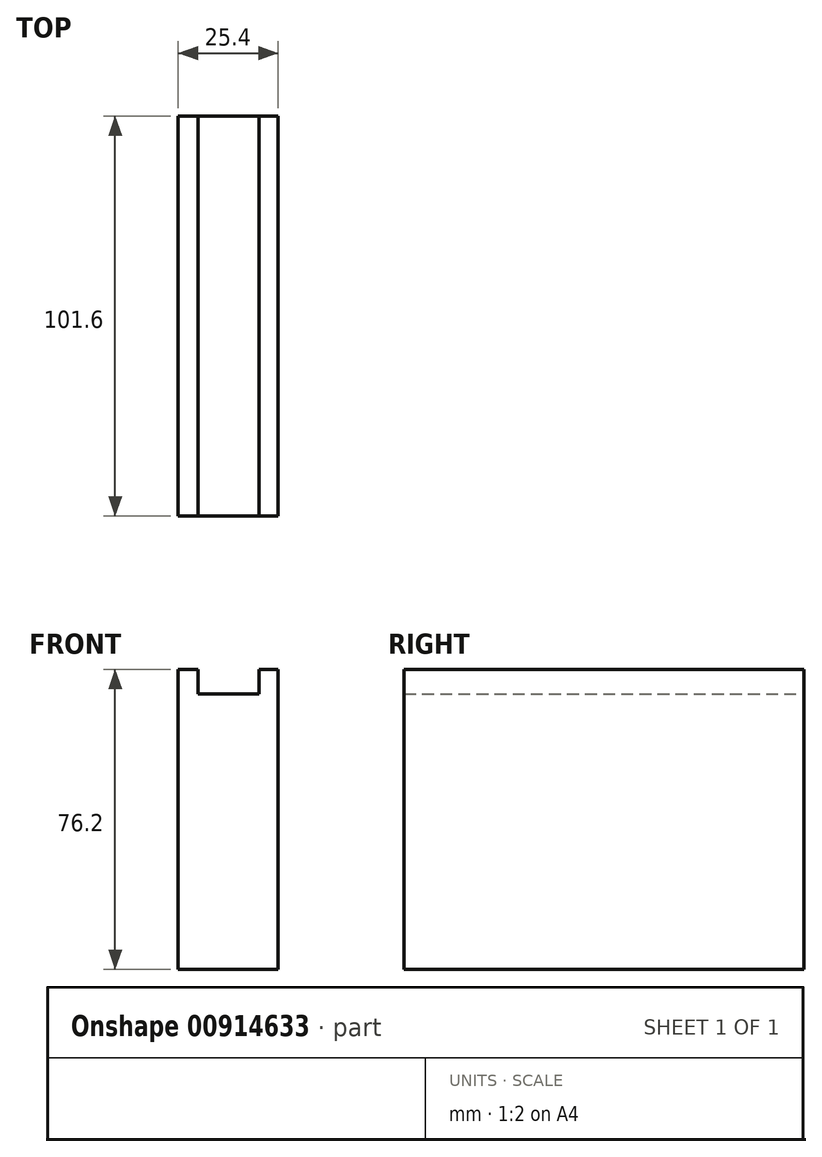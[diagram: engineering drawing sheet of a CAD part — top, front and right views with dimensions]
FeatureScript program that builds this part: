
annotation { "Feature Type Name" : "Feature", "Feature Type Description" : "" }
export const myFeature = defineFeature(function(context is Context, id is Id, definition is map)
    precondition{}
    {
        {
            var Q0;
            Q0=qCreatedBy(makeId("Right.planeOp"),FACE);
            var sketch = newSketch(context, id + "F0", { "sketchPlane" : qUnion([Q0])});
            skLineSegment(sketch, "E0.bottom", {"start": v(-44.25, 27.35) * mm, "end": v(57.35, 27.35) * mm});
            skLineSegment(sketch, "E0.top", {"start": v(-44.25, -48.85) * mm, "end": v(57.35, -48.85) * mm});
            skLineSegment(sketch, "E0.left", {"start": v(-44.25, 27.35) * mm, "end": v(-44.25, -48.85) * mm});
            skLineSegment(sketch, "E0.right", {"start": v(57.35, 27.35) * mm, "end": v(57.35, -48.85) * mm});
            skLineSegment(sketch, "E1.bottom", {"start": v(-44.25, 21.14) * mm, "end": v(57.35, 21.14) * mm});
            skLineSegment(sketch, "E1.left", {"start": v(-44.25, 21.14) * mm, "end": v(-44.25, -48.85) * mm});
            skLineSegment(sketch, "E1.right", {"start": v(57.35, 21.14) * mm, "end": v(57.35, -48.85) * mm});
            skSolve(sketch);
        }
        {
            var Q0;
            Q0 = qSketchRegion(id + "F0", true);
            extrude(context, id + "F1", {"entities" : qUnion([Q0]), "oppositeDirection" : true, "depth" : 5.08 * mm, "offsetDistance" : 25.4 * mm});
        }
        {
            var Q0;
            Q0=makeQuery(id+"F0.imprint","IMPRINT",FACE,{"disambiguationData":[TD([[makeQuery(id+"F0.imprint","IMPRINT",EDGE,{"derivedFrom":sQuery(id+"F0.wireOp",EDGE,"E1.bottom")}),-1.0]])]});
            extrude(context, id + "F2", {"entities" : qUnion([Q0]), "operationType" : NewBodyOperationType.ADD, "depth" : 15.5 * mm, "offsetDistance" : 25.4 * mm});
        }
        {
            var Q0;
            Q0 = qSketchRegion(id + "F0", true);
            extrude(context, id + "F3", {"entities" : qUnion([Q0]), "operationType" : NewBodyOperationType.ADD, "depth" : 20.32 * mm, "offsetDistance" : 25.4 * mm, "hasSecondDirection" : true, "secondDirectionOppositeDirection" : false, "secondDirectionDepth" : 15.5 * mm});
        }
    });
